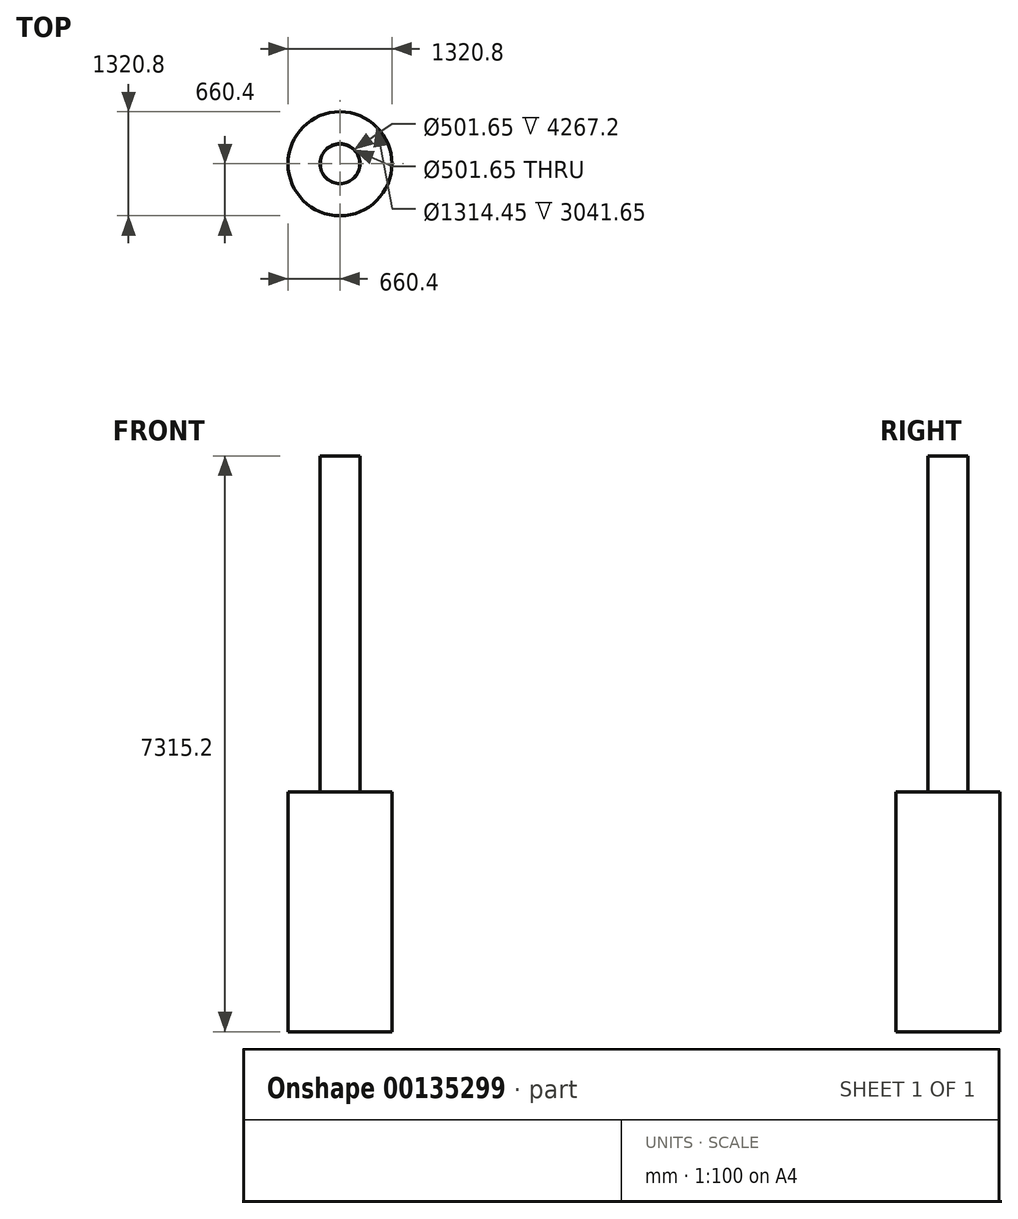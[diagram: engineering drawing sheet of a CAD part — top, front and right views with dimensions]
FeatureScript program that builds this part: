
annotation { "Feature Type Name" : "Feature", "Feature Type Description" : "" }
export const myFeature = defineFeature(function(context is Context, id is Id, definition is map)
    precondition{}
    {
        {
            var Q0;
            Q0=qCreatedBy(makeId("Top.planeOp"),FACE);
            var sketch = newSketch(context, id + "F0", { "sketchPlane" : qUnion([Q0])});
            skCircle(sketch, "E0", {"center": v(0, 0) * mm, "radius": 660.4 * mm});
            skSolve(sketch);
        }
        {
            var Q0;
            Q0=makeQuery(id+"F0.imprint","IMPRINT",FACE,{"disambiguationData":[TD([[makeQuery(id+"F0.imprint","IMPRINT",EDGE,{"derivedFrom":sQuery(id+"F0.wireOp",EDGE,"E0")}),1.0]])]});
            extrude(context, id + "F1", {"entities" : qUnion([Q0]), "depth" : 3.17 * mm});
        }
        {
            var Q0;
            Q0=makeQuery(id+"F1.opExtrude","CAP_FACE",FACE,{"disambiguationData":[OSD([sQuery(id+"F0.wireOp",EDGE,"E0")])],"isStart":false});
            var sketch = newSketch(context, id + "F2", { "sketchPlane" : qUnion([Q0])});
            skCircle(sketch, "E1.0", {"center": v(0, 0) * mm, "radius": 660.4 * mm});
            skCircle(sketch, "E2.0", {"center": v(0, 0) * mm, "radius": 657.22 * mm});
            skSolve(sketch);
        }
        {
            var Q0;
            Q0=makeQuery(id+"F2.imprint","IMPRINT",FACE,{"disambiguationData":[TD([[makeQuery(id+"F2.imprint","IMPRINT",EDGE,{"derivedFrom":sQuery(id+"F2.wireOp",EDGE,"E1.0")}),1.0]])]});
            extrude(context, id + "F3", {"entities" : qUnion([Q0]), "operationType" : NewBodyOperationType.ADD, "depth" : 3041.65 * mm});
        }
        {
            var Q0;
            Q0=makeQuery(id+"F3.opExtrude","CAP_FACE",FACE,{"disambiguationData":[OSD([sQuery(id+"F2.wireOp",EDGE,"E1.0"),sQuery(id+"F2.wireOp",EDGE,"E2.0")])],"isStart":false});
            var sketch = newSketch(context, id + "F4", { "sketchPlane" : qUnion([Q0])});
            skCircle(sketch, "E3.0", {"center": v(0, 0) * mm, "radius": 660.4 * mm});
            skSolve(sketch);
        }
        {
            var Q0;
            Q0=makeQuery(id+"F4.imprint","IMPRINT",FACE,{"disambiguationData":[TD([[makeQuery(id+"F4.imprint","IMPRINT",EDGE,{"derivedFrom":makeQuery(id+"F3.opExtrude","CAP_EDGE",EDGE,{"disambiguationData":[OSD([sQuery(id+"F2.wireOp",EDGE,"E2.0")])],"isStart":false})}),1.0]])]});
            var Q1;
            Q1=makeQuery(id+"F4.imprint","IMPRINT",FACE,{"disambiguationData":[TD([[makeQuery(id+"F4.imprint","IMPRINT",EDGE,{"derivedFrom":sQuery(id+"F4.wireOp",EDGE,"E3.0")}),1.0]])]});
            extrude(context, id + "F5", {"entities" : qUnion([Q0, Q1]), "operationType" : NewBodyOperationType.ADD, "depth" : 3.17 * mm});
        }
        {
            var Q0;
            Q0=makeQuery(id+"F5.opExtrude","CAP_FACE",FACE,{"disambiguationData":[OSD([sQuery(id+"F4.wireOp",EDGE,"E3.0")])],"isStart":false});
            var sketch = newSketch(context, id + "F6", { "sketchPlane" : qUnion([Q0])});
            skCircle(sketch, "E4.0", {"center": v(0, 0) * mm, "radius": 660.4 * mm});
            skCircle(sketch, "E5", {"center": v(0, 0) * mm, "radius": 254 * mm});
            skCircle(sketch, "E6", {"center": v(0, 0) * mm, "radius": 250.83 * mm});
            skSolve(sketch);
        }
        {
            var Q0;
            Q0=makeQuery(id+"F6.imprint","IMPRINT",FACE,{"disambiguationData":[TD([[makeQuery(id+"F6.imprint","IMPRINT",EDGE,{"derivedFrom":sQuery(id+"F6.wireOp",EDGE,"E6")}),1.0]])]});
            var Q1;
            Q1=makeQuery(id+"F1.opExtrude","SWEPT_BODY",BODY,{"disambiguationData":[OSD([sQuery(id+"F0.wireOp",EDGE,"E0")])]});
            extrude(context, id + "F7", {"entities" : qUnion([Q0]), "operationType" : NewBodyOperationType.REMOVE, "endBound" : BoundingType.UP_TO_BODY, "oppositeDirection" : true, "endBoundEntityBody" : qUnion([Q1]), "depth" : 25.4 * mm});
        }
        {
            var Q0;
            Q0=makeQuery(id+"F6.imprint","IMPRINT",FACE,{"disambiguationData":[TD([[makeQuery(id+"F6.imprint","IMPRINT",EDGE,{"derivedFrom":sQuery(id+"F6.wireOp",EDGE,"E5")}),1.0]])]});
            extrude(context, id + "F8", {"entities" : qUnion([Q0]), "depth" : 4267.2 * mm});
        }
    });
